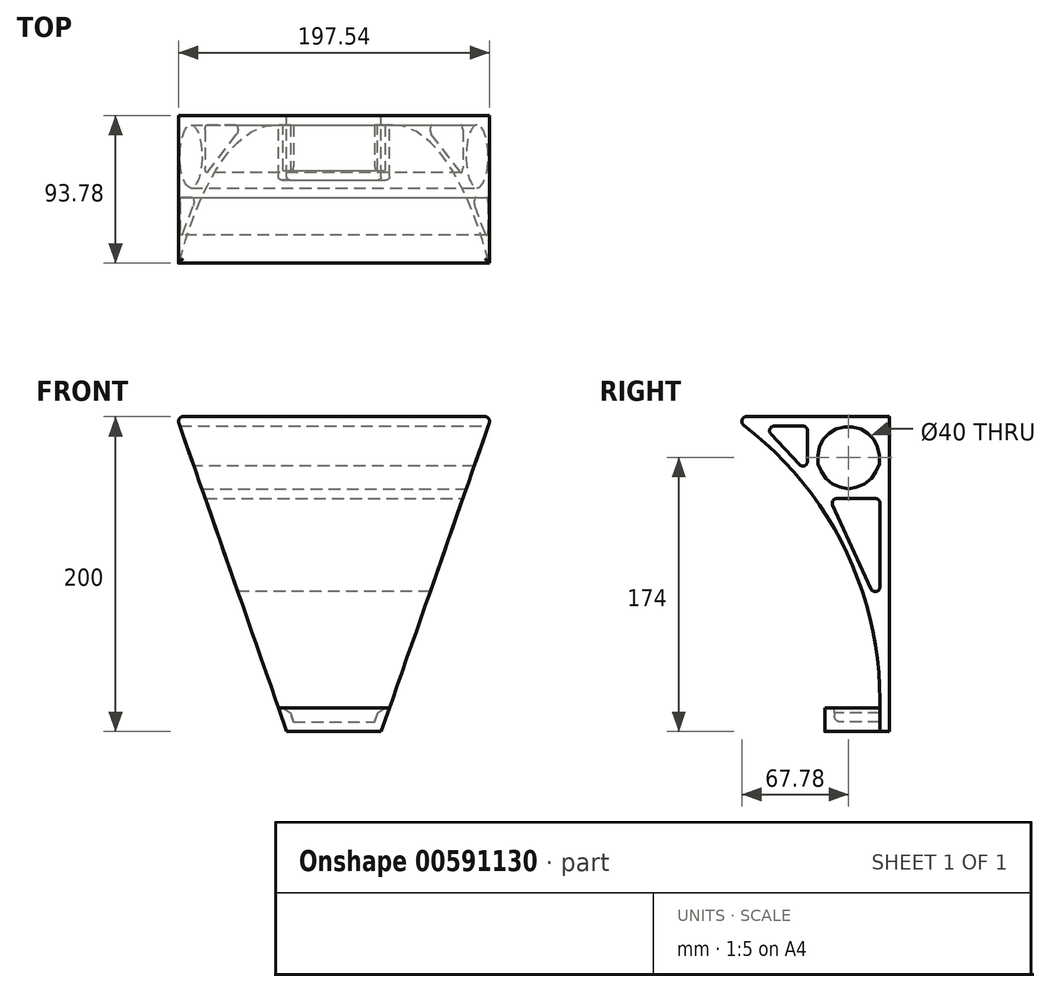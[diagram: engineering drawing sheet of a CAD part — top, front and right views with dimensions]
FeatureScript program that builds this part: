
annotation { "Feature Type Name" : "Feature", "Feature Type Description" : "" }
export const myFeature = defineFeature(function(context is Context, id is Id, definition is map)
    precondition{}
    {
        {
            var Q0;
            Q0=qCreatedBy(makeId("Front.planeOp"),FACE);
            var sketch = newSketch(context, id + "F0", { "sketchPlane" : qUnion([Q0])});
            skLineSegment(sketch, "E0", {"start": v(0, 0) * mm, "end": v(-30, 0) * mm});
            skLineSegment(sketch, "E1", {"start": v(-30, 0) * mm, "end": v(-100, 200) * mm});
            skLineSegment(sketch, "E2", {"start": v(-100, 200) * mm, "end": v(0, 200) * mm});
            skLineSegment(sketch, "E3", {"start": v(0, 200) * mm, "end": v(0, 0) * mm});
            skSolve(sketch);
        }
        {
            var Q0;
            Q0=makeQuery(id+"F0.imprint","IMPRINT",FACE,{"disambiguationData":[TD([[makeQuery(id+"F0.imprint","IMPRINT",EDGE,{"derivedFrom":sQuery(id+"F0.wireOp",EDGE,"E0")}),-1.0]])]});
            extrude(context, id + "F1", {"entities" : qUnion([Q0]), "depth" : 100 * mm, "offsetDistance" : 25 * mm});
        }
        {
            var Q0;
            Q0=makeQuery(id+"F1.opExtrude","SWEPT_FACE",FACE,{"disambiguationData":[OSD([sQuery(id+"F0.wireOp",EDGE,"E3")])]});
            var sketch = newSketch(context, id + "F2", { "sketchPlane" : qUnion([Q0])});
            skLineSegment(sketch, "E4", {"start": v(-100, 0) * mm, "end": v(-6, 0) * mm});
            skLineSegment(sketch, "E5", {"start": v(-6, 0) * mm, "end": v(-6, 20) * mm});
            skLineSegment(sketch, "E6", {"start": v(-100, 0) * mm, "end": v(-100, 200) * mm});
            skArc(sketch, "E7", {"start": v(-6, 20) * mm, "mid": v(-30.92, 121.53) * mm, "end": v(-100, 200) * mm});
            skCircle(sketch, "E8", {"center": v(-26, 174) * mm, "radius": 20 * mm});
            skLineSegment(sketch, "E9", {"start": v(-38, 148) * mm, "end": v(-6, 148) * mm});
            skLineSegment(sketch, "E10", {"start": v(-6, 148) * mm, "end": v(-6, 78) * mm});
            skLineSegment(sketch, "E11", {"start": v(-6, 78) * mm, "end": v(-38, 148) * mm});
            skLineSegment(sketch, "E12", {"start": v(-80, 194) * mm, "end": v(-52, 194) * mm});
            skLineSegment(sketch, "E13", {"start": v(-52, 194) * mm, "end": v(-52, 164) * mm});
            skLineSegment(sketch, "E14", {"start": v(-52, 164) * mm, "end": v(-80, 194) * mm});
            skSolve(sketch);
        }
        {
            var Q0;
            Q0 = qSketchRegion(id + "F2", true);
            extrude(context, id + "F3", {"entities" : qUnion([Q0]), "operationType" : NewBodyOperationType.REMOVE, "endBound" : BoundingType.THROUGH_ALL, "oppositeDirection" : true, "depth" : 25 * mm, "offsetDistance" : 25 * mm});
        }
        {
            var Q0;
            Q0=makeQuery(id+"F1.opExtrude","SWEPT_FACE",FACE,{"disambiguationData":[OSD([sQuery(id+"F0.wireOp",EDGE,"E3")])]});
            var sketch = newSketch(context, id + "F4", { "sketchPlane" : qUnion([Q0])});
            skLineSegment(sketch, "E15", {"start": v(-6, 0) * mm, "end": v(-41, 0) * mm});
            skLineSegment(sketch, "E16", {"start": v(-41, 0) * mm, "end": v(-41, 15) * mm});
            skLineSegment(sketch, "E17", {"start": v(-41, 15) * mm, "end": v(-35, 15) * mm});
            skLineSegment(sketch, "E18", {"start": v(-35, 15) * mm, "end": v(-35, 6) * mm});
            skLineSegment(sketch, "E19", {"start": v(-35, 6) * mm, "end": v(-6, 6) * mm});
            skLineSegment(sketch, "E20", {"start": v(-6, 6) * mm, "end": v(-6, 0) * mm});
            skSolve(sketch);
        }
        {
            var Q0;
            Q0=makeQuery(id+"F4.imprint","IMPRINT",FACE,{"disambiguationData":[TD([[makeQuery(id+"F4.imprint","IMPRINT",EDGE,{"derivedFrom":sQuery(id+"F4.wireOp",EDGE,"E15")}),-1.0]])]});
            extrude(context, id + "F5", {"entities" : qUnion([Q0]), "operationType" : NewBodyOperationType.ADD, "oppositeDirection" : true, "depth" : 40 * mm, "offsetDistance" : 25 * mm});
        }
        {
            var Q0;
            Q0=makeQuery(id+"F5.opExtrude","SWEPT_FACE",FACE,{"disambiguationData":[OSD([sQuery(id+"F4.wireOp",EDGE,"E20")])]});
            var sketch = newSketch(context, id + "F6", { "sketchPlane" : qUnion([Q0])});
            skLineSegment(sketch, "E21", {"start": v(40, 0) * mm, "end": v(30, 0) * mm});
            skLineSegment(sketch, "E22", {"start": v(30, 0) * mm, "end": v(35.26, 15) * mm});
            skLineSegment(sketch, "E23", {"start": v(35.26, 15) * mm, "end": v(40, 15) * mm});
            skLineSegment(sketch, "E24", {"start": v(40, 15) * mm, "end": v(40, 0) * mm});
            skSolve(sketch);
        }
        {
            var Q0;
            Q0 = qSketchRegion(id + "F6", true);
            extrude(context, id + "F7", {"entities" : qUnion([Q0]), "operationType" : NewBodyOperationType.REMOVE, "endBound" : BoundingType.THROUGH_ALL, "oppositeDirection" : true, "depth" : 25 * mm, "offsetDistance" : 25 * mm});
        }
        {
            var Q0;
            Q0=makeQuery(id+"F5.opExtrude","SWEPT_FACE",FACE,{"disambiguationData":[OSD([sQuery(id+"F4.wireOp",EDGE,"E18")])]});
            var sketch = newSketch(context, id + "F8", { "sketchPlane" : qUnion([Q0])});
            skLineSegment(sketch, "E25", {"start": v(32.1, 6) * mm, "end": v(35.26, 15) * mm});
            skLineSegment(sketch, "E26", {"start": v(35.26, 15) * mm, "end": v(28.9, 15) * mm});
            skLineSegment(sketch, "E27", {"start": v(28.9, 15) * mm, "end": v(25.75, 6) * mm});
            skLineSegment(sketch, "E28", {"start": v(25.75, 6) * mm, "end": v(32.1, 6) * mm});
            skSolve(sketch);
        }
        {
            var Q0;
            Q0=makeQuery(id+"F8.imprint","IMPRINT",FACE,{"disambiguationData":[TD([[makeQuery(id+"F8.imprint","IMPRINT",EDGE,{"derivedFrom":sQuery(id+"F8.wireOp",EDGE,"E25")}),-1.0]])]});
            extrude(context, id + "F9", {"entities" : qUnion([Q0]), "operationType" : NewBodyOperationType.ADD, "depth" : 29 * mm, "offsetDistance" : 25 * mm});
        }
        {
            var Q0;
            Q0=makeQuery(id+"F5.opExtrude","SWEPT_EDGE",EDGE,{"disambiguationData":[OSD([sQuery(id+"F4.wireOp",EDGE,"E18"),sQuery(id+"F4.wireOp",EDGE,"E19")])]});
            var Q1;
            {var subQ0=sQuery(id+"F2.wireOp",EDGE,"E5");var subQ1=sQuery(id+"F4.wireOp",EDGE,"E19");Q1=makeQuery(id+"F5.boolean.opBoolean","SPLIT",EDGE,{"disambiguationData":[topologyDisambiguationEdgeConnected([makeQuery(id+"F3.boolean.opBoolean","COPY",FACE,{"derivedFrom":makeQuery(id+"F3.opExtrude","SWEPT_FACE",FACE,{"disambiguationData":[OSD([subQ0])]})})])],"derivedFrom":makeQuery(id+"F5.opExtrude","SWEPT_EDGE",EDGE,{"disambiguationData":[OSD([subQ0,subQ1,sQuery(id+"F4.wireOp",EDGE,"E20")])]})});}
            fillet(context, id + "F10", {"entities" : qUnion([Q0, Q1]), "radius" : 4 * mm, "tangentPropagation" : true, "allowEdgeOverflow" : false});
        }
        {
            var Q0;
            Q0=makeQuery(id+"F3.boolean.opBoolean","COPY",EDGE,{"derivedFrom":makeQuery(id+"F3.opExtrude","SWEPT_EDGE",EDGE,{"disambiguationData":[OSD([sQuery(id+"F2.wireOp",EDGE,"E12"),sQuery(id+"F2.wireOp",EDGE,"E13")])]})});
            var Q1;
            Q1=makeQuery(id+"F3.boolean.opBoolean","COPY",EDGE,{"derivedFrom":makeQuery(id+"F3.opExtrude","SWEPT_EDGE",EDGE,{"disambiguationData":[OSD([sQuery(id+"F2.wireOp",EDGE,"E9"),sQuery(id+"F2.wireOp",EDGE,"E10")])]})});
            var Q2;
            Q2=makeQuery(id+"F3.boolean.opBoolean","COPY",EDGE,{"derivedFrom":makeQuery(id+"F3.opExtrude","SWEPT_EDGE",EDGE,{"disambiguationData":[OSD([sQuery(id+"F2.wireOp",EDGE,"E9"),sQuery(id+"F2.wireOp",EDGE,"E11")])]})});
            var Q3;
            Q3=makeQuery(id+"F3.boolean.opBoolean","COPY",EDGE,{"derivedFrom":makeQuery(id+"F3.opExtrude","SWEPT_EDGE",EDGE,{"disambiguationData":[OSD([sQuery(id+"F2.wireOp",EDGE,"E12"),sQuery(id+"F2.wireOp",EDGE,"E14")])]})});
            var Q4;
            Q4=makeQuery(id+"F3.boolean.opBoolean","COPY",EDGE,{"derivedFrom":makeQuery(id+"F3.opExtrude","SWEPT_EDGE",EDGE,{"disambiguationData":[OSD([sQuery(id+"F2.wireOp",EDGE,"E13"),sQuery(id+"F2.wireOp",EDGE,"E14")])]})});
            var Q5;
            Q5=makeQuery(id+"F3.boolean.opBoolean","COPY",EDGE,{"derivedFrom":makeQuery(id+"F3.opExtrude","SWEPT_EDGE",EDGE,{"disambiguationData":[OSD([sQuery(id+"F2.wireOp",EDGE,"E10"),sQuery(id+"F2.wireOp",EDGE,"E11")])]})});
            fillet(context, id + "F11", {"entities" : qUnion([Q0, Q1, Q2, Q3, Q4, Q5]), "radius" : 3 * mm, "tangentPropagation" : true, "allowEdgeOverflow" : false});
        }
        {
            var Q0;
            Q0=makeQuery(id+"F1.opExtrude","SWEPT_BODY",BODY,{"disambiguationData":[OSD([sQuery(id+"F0.wireOp",EDGE,"E0"),sQuery(id+"F0.wireOp",EDGE,"E1"),sQuery(id+"F0.wireOp",EDGE,"E2"),sQuery(id+"F0.wireOp",EDGE,"E3")])]});
            var Q1;
            Q1=makeQuery(id+"F5.boolean.opBoolean","MERGE",FACE,{"derivedFrom":[makeQuery(id+"F1.opExtrude","SWEPT_FACE",FACE,{"disambiguationData":[OSD([sQuery(id+"F0.wireOp",EDGE,"E3")])]}),makeQuery(id+"F5.opExtrude","CAP_FACE",FACE,{"disambiguationData":[OSD([sQuery(id+"F4.wireOp",EDGE,"E15"),sQuery(id+"F4.wireOp",EDGE,"E16"),sQuery(id+"F4.wireOp",EDGE,"E17"),sQuery(id+"F4.wireOp",EDGE,"E18"),sQuery(id+"F4.wireOp",EDGE,"E19"),sQuery(id+"F4.wireOp",EDGE,"E20")])],"isStart":true})]});
            mirror(context, id + "F12", {"operationType" : NewBodyOperationType.ADD, "entities" : qUnion([Q0]), "mirrorPlane" : qUnion([Q1])});
        }
        {
            var Q0;
            Q0=makeQuery(id+"F9.opExtrude","SWEPT_EDGE",EDGE,{"disambiguationData":[OSD([sQuery(id+"F4.wireOp",EDGE,"E17"),sQuery(id+"F4.wireOp",EDGE,"E18"),sQuery(id+"F8.wireOp",EDGE,"E26"),sQuery(id+"F8.wireOp",EDGE,"E27")])]});
            var Q1;
            Q1=makeQuery(id+"F12.opPattern","COPY",EDGE,{"derivedFrom":makeQuery(id+"F9.opExtrude","SWEPT_EDGE",EDGE,{"disambiguationData":[OSD([sQuery(id+"F4.wireOp",EDGE,"E17"),sQuery(id+"F4.wireOp",EDGE,"E18"),sQuery(id+"F8.wireOp",EDGE,"E26"),sQuery(id+"F8.wireOp",EDGE,"E27")])]}),"instanceName":"1"});
            chamfer(context, id + "F13", {"entities" : qUnion([Q0, Q1]), "width" : 5 * mm, "tangentPropagation" : true});
        }
        {
            var Q0;
            {var subQ0=sQuery(id+"F0.wireOp",EDGE,"E2");var subQ1=makeQuery(id+"F3.boolean.opBoolean","MERGE",EDGE,{"derivedFrom":[makeQuery(id+"F1.opExtrude","CAP_EDGE",EDGE,{"disambiguationData":[OSD([subQ0])],"isStart":false}),makeQuery(id+"F3.opExtrude","SWEPT_EDGE",EDGE,{"disambiguationData":[OSD([subQ0,sQuery(id+"F0.wireOp",EDGE,"E3"),sQuery(id+"F2.wireOp",EDGE,"E6"),sQuery(id+"F2.wireOp",EDGE,"E7")])]})]});Q0=makeQuery(id+"F12.boolean.opBoolean","MERGE",EDGE,{"derivedFrom":[subQ1,makeQuery(id+"F12.opPattern","COPY",EDGE,{"derivedFrom":subQ1,"instanceName":"1"})]});}
            var Q1;
            Q1=makeQuery(id+"F12.opPattern","COPY",EDGE,{"derivedFrom":makeQuery(id+"F1.opExtrude","SWEPT_EDGE",EDGE,{"disambiguationData":[OSD([sQuery(id+"F0.wireOp",EDGE,"E1"),sQuery(id+"F0.wireOp",EDGE,"E2")])]}),"instanceName":"1"});
            var Q2;
            Q2=makeQuery(id+"F1.opExtrude","SWEPT_EDGE",EDGE,{"disambiguationData":[OSD([sQuery(id+"F0.wireOp",EDGE,"E1"),sQuery(id+"F0.wireOp",EDGE,"E2")])]});
            fillet(context, id + "F14", {"entities" : qUnion([Q0, Q1, Q2]), "radius" : 3 * mm, "tangentPropagation" : true, "allowEdgeOverflow" : false});
        }
        {
            var Q0;
            Q0=makeQuery(id+"F7.boolean.opBoolean","INTERSECT",EDGE,{"derivedFrom":[makeQuery(id+"F5.opExtrude","SWEPT_FACE",FACE,{"disambiguationData":[OSD([sQuery(id+"F4.wireOp",EDGE,"E16")])]}),makeQuery(id+"F7.opExtrude","SWEPT_FACE",FACE,{"disambiguationData":[OSD([sQuery(id+"F6.wireOp",EDGE,"E22")])]})]});
            var Q1;
            Q1=makeQuery(id+"F12.opPattern","COPY",EDGE,{"derivedFrom":makeQuery(id+"F7.boolean.opBoolean","INTERSECT",EDGE,{"derivedFrom":[makeQuery(id+"F5.opExtrude","SWEPT_FACE",FACE,{"disambiguationData":[OSD([sQuery(id+"F4.wireOp",EDGE,"E16")])]}),makeQuery(id+"F7.opExtrude","SWEPT_FACE",FACE,{"disambiguationData":[OSD([sQuery(id+"F6.wireOp",EDGE,"E22")])]})]}),"instanceName":"1"});
            fillet(context, id + "F15", {"entities" : qUnion([Q0, Q1]), "radius" : 2 * mm, "tangentPropagation" : true, "allowEdgeOverflow" : false});
        }
    });
